# Revit family: Boiling Water System-Rheem-Lazer Commercial1
name_source: partatom
category: Mechanical Equipment
revit_build: Autodesk Revit Architecture 2012 (Build: 20110309_2315(x64)
units: mm (PartAtom-declared; Revit-internal decimal feet)

## types (1)
- Lazer with Eco Button - 7.5L - White
    Apparent Load = 4600 VA
    Assembly Code = D3020100
    Commercial = No
    Connector Radius = 8 mm  [stored 0.0262467 ft]
    Default Elevation = 1200 mm
    Depth_ANZRS = 191 mm  [stored 0.62664 ft]
    Description = The Rheem Lazer is a very clever option with sleek but understated appearance and space saving over bench installation
    Economy = Yes
    Height_ANZRS = 515 mm  [stored 1.68963 ft]
    Keynote = HWU
    Manufacturer = Rheem Australia Pty Ltd
    Material_ANZRS = Metal-Powdercoat-White-Rheem
    Model = 70307W
    Outlet Base Offset = 58 mm  [stored 0.190289 ft]
    Outlet Position = 269 mm  [stored 0.882546 ft]
    Type Comments = Initial delivery 50 cups with recovery 123 cups per hour
    URL = www.rheem.com.au
    Width_ANZRS = 334 mm  [stored 1.0958 ft]

note: [stored X ft] marks values corroborated as IEEE doubles in the binary element streams (Revit-internal decimal feet)

## geometry (parser evidence)
native form markers: Blend x8, Sweep x1
no freeform markers — native parametric forms only
